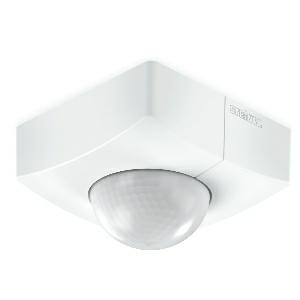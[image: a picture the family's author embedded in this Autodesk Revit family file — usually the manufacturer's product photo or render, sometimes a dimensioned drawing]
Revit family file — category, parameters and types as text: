
# Revit family: is_345_010539
name_source: partatom
category: Elektroinstallationen
revit_build: Autodesk Revit 2016 (Build: 20190508_0715(x64)
units: mm (PartAtom-declared; Revit-internal decimal feet)

## family parameters
Basisbauteil = Fläche
Beim Laden mit Abzugskörper schneiden = Nein
Bemaßung runder Anschluss = Durchmesser verwenden
Beschriftungsausrichtung beibehalten = Nein
Gemeinsam genutzt = Nein
Raumberechnungspunkt = Nein
Teiletyp = Normal

## types (1)
- IS 345
    Apparent Load = 0 VA
    Beschreibung = Type: Motion detectors; Dimensions (L x W x H): 65 x 95 x 95 mm; Mains power supply: 220 – 240 V / 50 – 60 Hz; Sensor Technology: passive infrared; Application, place: Outdoors, Indoors; Application, room: corridor / aisle, multi-storey / underground car park, outdoors, Indoors; Installation site: ceiling; Installation: Surface wiring; Switching zones: 280 switching zones; Electronic scalability: No; Mechanical scalability: No; Mounting height: 2,50 – 5,00 m; Optimum mounting height: 2,8 m; Detection angle: 360 °; Angle of aperture: 45 °; Sneak-by guard: Yes; Capability of masking out individual segments: Yes; Reach, radial: 12 x 6 m (72 m²); Reach, tangential: 23 x 6 m (138 m²); Twilight setting TEACH: Yes; Twilight setting: 2 – 1000 lx; Time setting: 5 sec – 15 min; Constant-lighting control: No; Basic light level function: No; Functions: Normal / test mode, Manual ON / ON-OFF; Settings via: Remote control, Potentiometers, Smart Remote; With remote control: No; Interconnection: Yes; IP-rating: IP54; Material: Plastic; Ambient temperature: -20 – 50 °C; Colour: white; Colour, RAL: 9003; Manufacturer's Warranty: 5 years; Version: PF - surface, sq.; PU1, EAN: 4007841010539
    Height = 95 mm
    Hersteller = Steinel
    Length = 65 mm
    Maximum range = 11.589 m
    ModVariant = Nein
    Modell = 010539
    Mounting Place = Ceiling
    Mounting Type = Surface mounted
    Number of Poles = 1
    OnlyDefault = Ja
    Power Factor = 1
    Product Name = IS 345
    Product group = Sensor-switched outdoor light
    ProductGroupID = 3
    Protection Class = Protection class
    Protection Degree = IP 54
    RlxData = <blob elided: 163709 chars, md5=edbbf332>
    Sensor characteristics = Stretched
    Sensor type = Passive (infrared)
    SensorDataFile = <blob elided: 5885 chars, md5=98bccc25>
    Type of entry = Motion
    Typenbild = produkt1_010539.jpg
    Typenkommentare = Product without accessories
    URL = http://relux.com
    VarID = ---
    Voltage = 0 V
    Vorgabe-Ansicht = 1800 mm
    Weight = 0.00 kg
    Width = 95 mm

## geometry (parser evidence)
native form markers: Blend x4, Sweep x17
no freeform markers — native parametric forms only
